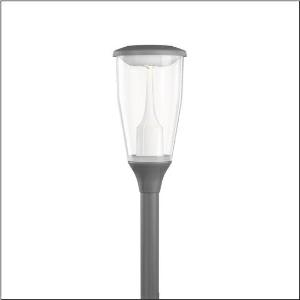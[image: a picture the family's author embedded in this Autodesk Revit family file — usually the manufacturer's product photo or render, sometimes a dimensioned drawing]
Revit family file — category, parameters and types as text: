
# Revit family: dl_11_iq___p1_0a_5xa5565nf14hp00022_fef3
name_source: partatom
category: Lighting Fixtures
units: mm (PartAtom-declared; Revit-internal decimal feet)

## family parameters
Cut with Voids When Loaded = No
Host = Face
Light Source = No
Part Type = Normal
Room Calculation Point = No
Round Connector Dimension = Use Diameter
Shared = No

## types (1)
- --- (1 x LED, 4280 lm, 33.6 W, 2700K)
    Apparent Load = 34 VA
    CIE Flux Codes = 33 63 91 94 100
    Color Rendering = 70
    Color Temperature = 2700K
    Default Elevation = 1800 mm
    Description = DL 11 iQ, mast luminaire, Module 540 iQ-SR, primary light control with 3 zone facetted reflector, of plastic, silver coated, highly specular, structured, primary optical cover: cover, of PMMA, transparent, light distribution: P1.0a, light emission: direct distribution, primary light characteristic: asymmetric, installation type: post-top, LED, High Power LED, light colour: 727, colour temperature: 2700K, control: Street-Remote, Auto-Match, Temp-Guard, Lumen-Switch, Night-Set, Smart-Wire, Light-Fading, Desk-Remote (wireless, voltage-free reading and setting of iQ features in the workshop via application-optimized NFC function/RFID function), optimised constant luminous flux control (CLO 2.0), mains connection: 220..240V, AC, 50/60Hz, connection cable pre-assembled, cable length: 5,5m, start of lifetime: 34W, end of service life: 36W, luminaire housing, upper part, of diecast aluminium, coated, Siteco® metallic grey (DB 702S), spigot size: 60mm (post-top), post-top mast mounting element, of diecast aluminium, coated, Siteco® metallic grey (DB 702S), Module 540 iQ-SR, traffic white (RAL 9016), equipment: Power, protection rating (complete): IP66, insulation class (complete): insulation class II (safety insulation), certification: CE, ENEC, ENEC+, VDE, packaging unit: 1 piece

Light Distribution: P1.0a
    Height = 665 mm
    Lamp = 1 x LED
    Lamp Light Flux = 4280 lm
    Lamp Power = 33.6 W
    Lamp count = 1
    Length = 334 mm
    Luminous efficacy = 127 lm/W
    Manufacturer = Siteco
    ModVariant = No
    Model = 5XA5565NF14HP00022
    Number of Poles = 1
    OnlyDefault = Yes
    Power Factor = 1
    Product Name = DL 11 iQ | P1.0a
    Product group = mast luminaire | pylon top
    ProductGroupID = 6100
    Protection Class = Protection class II
    Protection Degree = IP 66
    RLX_Detail_Level = 1
    RLX_Emergency_Light_Flux = 0 lm
    RLX_Emergency_Type = 0
    RLX_Emergency_Type_DB = No
    RlxData = <blob elided: 104189 chars, md5=be2896f6>
    Socket = socket
    Standby Power = 0 W
    System Light Flux = 4280 lm
    System Power = 34 W
    Type Comments = factory setting: luminous flux: 100 % | dim-lin: 254 | 695 mA
    Type Image = l_1258354.jpg
    URL = http://relux.com
    VarID = @adj_001737
    Voltage = 0 V
    Weight = 0.00 kg
    Width = 0 mm  [stored 0 ft]

note: [stored X ft] marks values corroborated as IEEE doubles in the binary element streams (Revit-internal decimal feet)

## geometry (parser evidence)
native form markers: Blend x4, Sweep x9
no freeform markers — native parametric forms only
